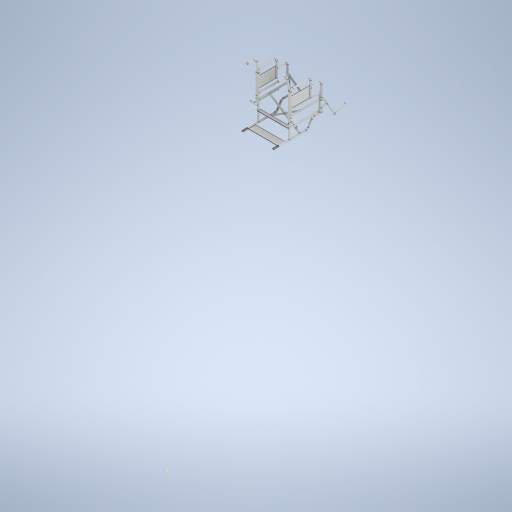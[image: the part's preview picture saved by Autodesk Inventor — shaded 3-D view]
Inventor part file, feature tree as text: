
AUTODESK INVENTOR PART (.ipt)
format: ipt  version: 2023 (Build 270158000, 158)  size: 1,103,872 bytes
history: native  units: in
note: dims shown in document units (in); Inventor stores cm internally (conversion verified against a paired STEP export)
features: sketch x32, plane x21, sweep x13, extrude x12, mirror x4
ambient origin geometry x8: Origin, YZ Plane, XZ Plane, XY Plane, X Axis, Y Axis, Z Axis, Center Point
bodies: Solid1 (feature_tree)
feature tree (82):
  sketch  "Sketch1"  dims[d14=3.5in d15=1.5in]
  plane  "Work Plane1"
  sweep  "Sweep1"
  sweep  "Sweep2"
  sweep  "Sweep3"
  sketch  "Sketch5"  dims[d22=17.0in d23=6.0in]
  plane  "Work Plane2"
  sweep  "Sweep4"
  plane  "Work Plane3"
  sweep  "Sweep5"
  plane  "Work Plane4"
  sweep  "Sweep6"
  sweep  "Sweep7"
  plane  "Work Plane5"
  sweep  "Sweep8"
  extrude  "Extrusion1"  Depth=9.8677in
  plane  "Work Plane6"
  sketch  "Sketch11"  dims[d37=0.0in d38=0.0in d39=0.0in d40=0.0in]
  plane  "Work Plane7"
  sketch  "Sketch12"  dims[d41=0.875in d42=0.0in d43=0.0in]
  plane  "Work Plane8"
  sweep  "Sweep9"
  sweep  "Sweep10"
  plane  "Work Plane9"
  extrude  "Extrusion2"  TaperAngle=0.0deg  [1 undecoded]
  plane  "Work Plane10"
  mirror  "Mirror1"
  sketch  "Sketch18"  dims[d50=0.875in d51=0.0in d52=0.0in]
  extrude  "Extrusion4"  TaperAngle=0.0deg  [1 undecoded]
  extrude  "Extrusion5"  TaperAngle=0.0deg  [1 undecoded]
  plane  "Work Plane13"
  mirror  "Mirror2"
  plane  "Work Plane14"
  extrude  "Extrusion6"  TaperAngle=0.0deg  [1 undecoded]
  extrude  "Extrusion7"  TaperAngle=0.0deg  [1 undecoded]
  sketch  "Sketch23"  dims[d63=17.0in d64=0.875in]
  plane  "Work Plane15"
  sketch  "Sketch24"  dims[d65=0.875in d66=0.0in d67=0.0in]
  sweep  "Sweep11"
  plane  "Work Plane16"
  sketch  "Sketch25"  dims[d68=0.0in d69=0.0in d70=0.875in]
  sketch  "Sketch26"  dims[d71=0.875in d72=0.75in]
  sweep  "Sweep12"
  extrude  "Extrusion8"  Depth=11.0in
  mirror  "Mirror3"
  plane  "Work Plane17"
  extrude  "Extrusion9"  Depth=0.875in
  plane  "Work Plane18"
  extrude  "Extrusion10"  TaperAngle=0.0deg  [1 undecoded]
  plane  "Work Plane19"
  extrude  "Extrusion11"  Depth=0.875in
  plane  "Work Plane20"
  sketch  "Sketch31"  dims[d93=0.875in]
  plane  "Work Plane21"
  extrude  "Extrusion12"  Depth=0.75in
  extrude  "Extrusion13"  Depth=2.8125in TaperAngle=0.0deg
  sketch  "Sketch33"  dims[d95=1.5in d96=0.0in]
  plane  "Work Plane22"
  sketch  "Sketch34"  dims[d97=0.875in]
  plane  "Work Plane23"
  sweep  "Sweep13"
  mirror  "Mirror4"
  sketch  "Sketch2"  dims[d16=6.0in d17=3.0in]
  sketch  "Sketch3"  dims[d18=30.0deg d19=0.6871in]
  sketch  "Sketch4"  dims[d20=6.0in d21=16.0in]
  sketch  "Sketch6"  dims[d24=17.0in d25=9.5in]
  sketch  "Sketch7"  dims[d26=10.0in d28=1.5in]
  sketch  "Sketch8"  dims[d29=1.5in d30=3.0in]
  sketch  "Sketch9"  dims[d31=31.0in d33=9.8677in]
  sketch  "Sketch10"  dims[d34=0.875in d35=0.0in d36=0.0in]
  sketch  "Sketch13"  dims[d44=0.875in d45=0.0in d46=0.0in]
  sketch  "Sketch14"  dims[d47=0.875in d48=0.0in d49=0.0in]
  sketch  "Sketch19"  dims[d53=0.875in d54=0.0in d55=0.0in]
  sketch  "Sketch20"  dims[d56=0.75in d57=0.875in]
  sketch  "Sketch21"  dims[d58=8.0in d59=4.0in d60=0.0in]
  sketch  "Sketch22"  dims[d61=-12.0in d62=11.0in]
  sketch  "Sketch27"  dims[d73=2.0in d74=0.0in d86=2.8125in d87=0.0in]
  sketch  "Sketch28"  dims[d88=0.5in d89=4.5in d90=0.0in]
  sketch  "Sketch29"  dims[d91=0.875in]
  sketch  "Sketch30"  dims[d92=0.75in]
  sketch  "Sketch32"  dims[d94=0.75in]
  sketch  "Sketch35"  dims[d98=0.75in d99=1.5in d100=0.0in d102=12.0in d103=1.0in d104=11.0in d105=4.75in d106=4.5in d107=0.0in d108=0.0in d109=0.0in d110=0.0in d111=6.0in d112=0.0in d113=0.02in d114=0.0in d115=5.105in d116=0.0in d117=9.5825in d118=0.0in d119=0.0591in d120=3.937in d121=0.0591in d122=3.937in d123=16.4562in d124=0.0in d125=2.0282in d126=0.7874in d127=90.0deg d128=0.7874in d129=16.125in d130=0.0in d131=90.0deg d132=90.0deg d133=90.0deg d134=90.0deg d135=16.125in d136=0.0in d137=13.3858in d138=90.0deg d139=0.875in d140=0.0in d141=0.0in d81=0.0197in d82=0.0344in d83=0.0197in d84=0.0344in]
note: 6 required parameter values undecoded (feature->parameter linkage not recoverable at this tier; creation-order binding heuristic only, values carry confidence <= 0.55)
